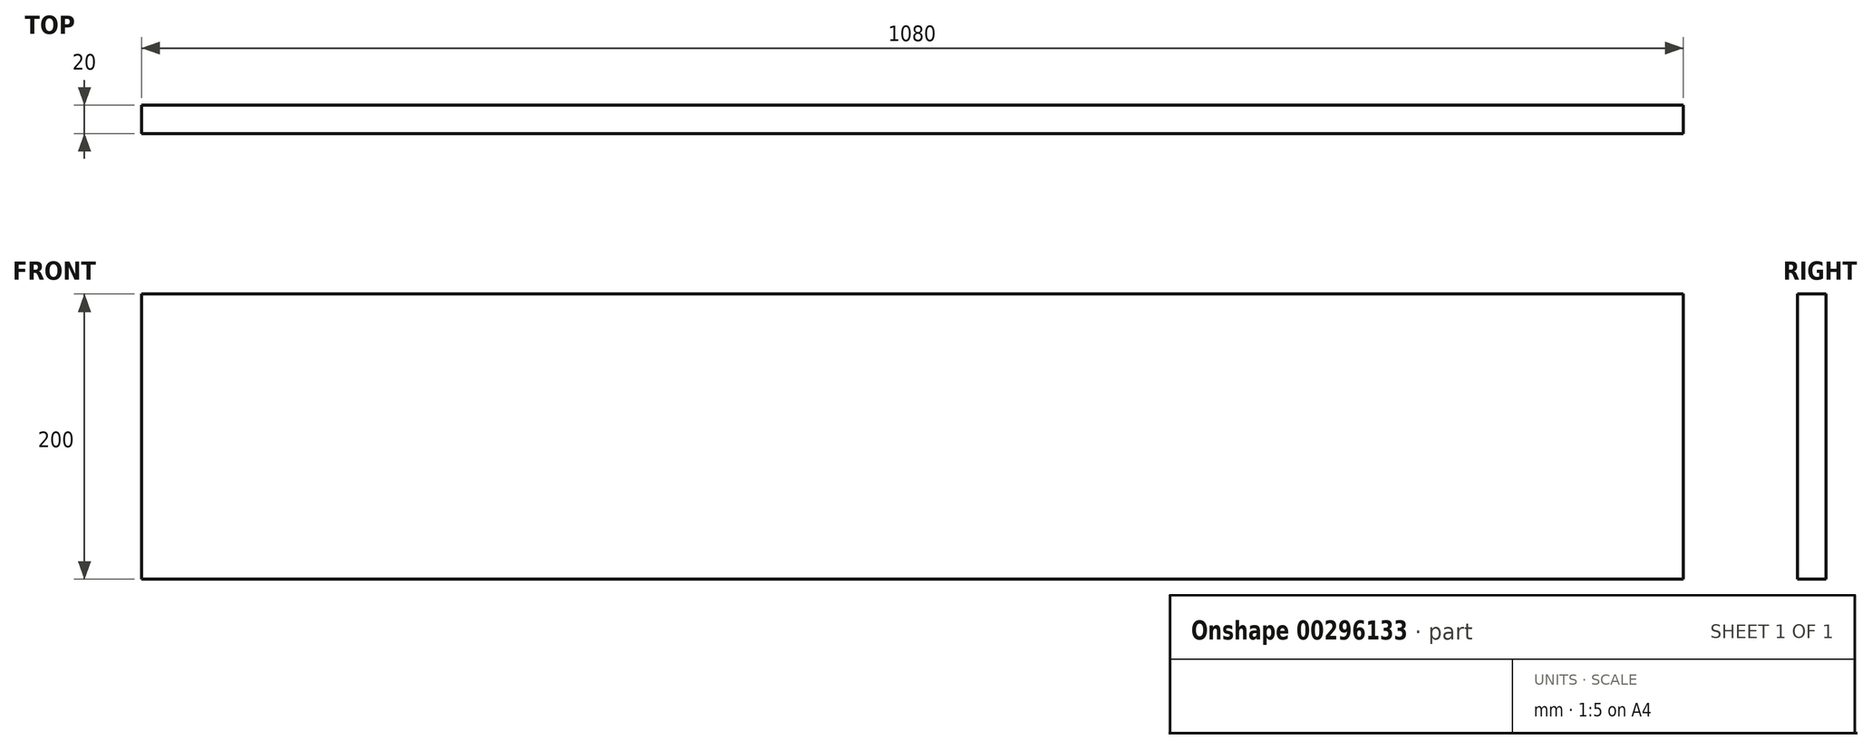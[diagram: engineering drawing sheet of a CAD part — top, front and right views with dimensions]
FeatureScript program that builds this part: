
annotation { "Feature Type Name" : "Feature", "Feature Type Description" : "" }
export const myFeature = defineFeature(function(context is Context, id is Id, definition is map)
    precondition{}
    {
        {
            var Q0;
            Q0=qCreatedBy(makeId("Front.planeOp"),FACE);
            var sketch = newSketch(context, id + "F0", { "sketchPlane" : qUnion([Q0])});
            skLineSegment(sketch, "E0.bottom", {"start": v(540, 100) * mm, "end": v(-540, 100) * mm});
            skLineSegment(sketch, "E0.top", {"start": v(540, -100) * mm, "end": v(-540, -100) * mm});
            skLineSegment(sketch, "E0.left", {"start": v(540, 100) * mm, "end": v(540, -100) * mm});
            skLineSegment(sketch, "E0.right", {"start": v(-540, 100) * mm, "end": v(-540, -100) * mm});
            skPoint(sketch, "E0.middle", {"position": v(0, 0) * mm});
            skSolve(sketch);
        }
        {
            var Q0;
            Q0=makeQuery(id+"F0.imprint","IMPRINT",FACE,{"disambiguationData":[TD([[makeQuery(id+"F0.imprint","IMPRINT",EDGE,{"derivedFrom":sQuery(id+"F0.wireOp",EDGE,"E0.bottom")}),1.0]])]});
            extrude(context, id + "F1", {"entities" : qUnion([Q0]), "oppositeDirection" : true, "depth" : 20 * mm});
        }
    });
